annotation { "Feature Type Name" : "Feature", "Feature Type Description" : "" }
export const myFeature = defineFeature(function(context is Context, id is Id, definition is map)
    precondition{}
    {
        {
            var Q0;
            Q0=qCreatedBy(makeId("Front.planeOp"),FACE);
            var sketch = newSketch(context, id + "F0", { "sketchPlane" : qUnion([Q0])});
            skLineSegment(sketch, "E0", {"start": v(0, 0) * mm, "end": v(-4572, 0) * mm});
            skLineSegment(sketch, "E1", {"start": v(0, 0) * mm, "end": v(4572, 0) * mm});
            skLineSegment(sketch, "E2", {"start": v(0, 0) * mm, "end": v(0, 2286) * mm, "construction": true});
            skLineSegment(sketch, "E3", {"start": v(0, 2286) * mm, "end": v(-4572, 0) * mm});
            skLineSegment(sketch, "E4", {"start": v(0, 2286) * mm, "end": v(4572, 0) * mm});
            skLineSegment(sketch, "E5", {"start": v(-4572, 0) * mm, "end": v(-5486.4, 0) * mm});
            skLineSegment(sketch, "E6", {"start": v(-5486.4, 0) * mm, "end": v(0, 2743.2) * mm});
            skLineSegment(sketch, "E7", {"start": v(4572, 0) * mm, "end": v(5486.4, 0) * mm});
            skLineSegment(sketch, "E8", {"start": v(5486.4, 0) * mm, "end": v(0, 2743.2) * mm});
            skLineSegment(sketch, "E9", {"start": v(0, 2286) * mm, "end": v(0, 2743.2) * mm});
            skLineSegment(sketch, "E10", {"start": v(-4572, 0) * mm, "end": v(-4572, -3352.8) * mm});
            skLineSegment(sketch, "E11", {"start": v(-4572, -3352.8) * mm, "end": v(4572, -3352.8) * mm});
            skLineSegment(sketch, "E12", {"start": v(4572, -3352.8) * mm, "end": v(4572, 0) * mm});
            skLineSegment(sketch, "E13", {"start": v(-4572, -3352.8) * mm, "end": v(-4572, -3962.4) * mm});
            skLineSegment(sketch, "E14", {"start": v(-4572, -3962.4) * mm, "end": v(4572, -3962.4) * mm});
            skLineSegment(sketch, "E15", {"start": v(4572, -3962.4) * mm, "end": v(4572, -3352.8) * mm});
            skLineSegment(sketch, "E16", {"start": v(4572, -3352.8) * mm, "end": v(9144, -3352.8) * mm});
            skLineSegment(sketch, "E17", {"start": v(9144, -3352.8) * mm, "end": v(9144, -3962.4) * mm});
            skLineSegment(sketch, "E18", {"start": v(9144, -3962.4) * mm, "end": v(4572, -3962.4) * mm});
            skLineSegment(sketch, "E19.bottom", {"start": v(6096, -1219.2) * mm, "end": v(7315.2, -1219.2) * mm});
            skLineSegment(sketch, "E19.top", {"start": v(6096, -2743.2) * mm, "end": v(7315.2, -2743.2) * mm});
            skLineSegment(sketch, "E19.left", {"start": v(6096, -1219.2) * mm, "end": v(6096, -2743.2) * mm});
            skLineSegment(sketch, "E19.right", {"start": v(7315.2, -1219.2) * mm, "end": v(7315.2, -2743.2) * mm});
            skLineSegment(sketch, "E20", {"start": v(6096, -2743.2) * mm, "end": v(4572, -2743.2) * mm, "construction": true});
            skLineSegment(sketch, "E21", {"start": v(6248.4, -1371.6) * mm, "end": v(7162.8, -1371.6) * mm});
            skLineSegment(sketch, "E22", {"start": v(7162.8, -1371.6) * mm, "end": v(7162.8, -2590.8) * mm});
            skLineSegment(sketch, "E23", {"start": v(7162.8, -2590.8) * mm, "end": v(6248.4, -2590.8) * mm});
            skLineSegment(sketch, "E24", {"start": v(6248.4, -2590.8) * mm, "end": v(6248.4, -1371.6) * mm});
            skLineSegment(sketch, "E25", {"start": v(609.6, -1371.6) * mm, "end": v(3352.8, -1371.6) * mm});
            skLineSegment(sketch, "E26", {"start": v(3352.8, -1371.6) * mm, "end": v(3352.8, -2743.2) * mm});
            skLineSegment(sketch, "E27", {"start": v(3352.8, -2743.2) * mm, "end": v(609.6, -2743.2) * mm});
            skLineSegment(sketch, "E28", {"start": v(609.6, -2743.2) * mm, "end": v(609.6, -1371.6) * mm});
            skLineSegment(sketch, "E29", {"start": v(762, -1524) * mm, "end": v(3200.4, -1524) * mm});
            skLineSegment(sketch, "E30", {"start": v(3200.4, -1524) * mm, "end": v(3200.4, -2590.8) * mm});
            skLineSegment(sketch, "E31", {"start": v(3200.4, -2590.8) * mm, "end": v(762, -2590.8) * mm});
            skLineSegment(sketch, "E32", {"start": v(762, -2590.8) * mm, "end": v(762, -1524) * mm});
            skLineSegment(sketch, "E33", {"start": v(-3352.8, -3352.8) * mm, "end": v(-3352.8, -1219.2) * mm});
            skLineSegment(sketch, "E34", {"start": v(-3352.8, -1219.2) * mm, "end": v(-2438.4, -1219.2) * mm});
            skLineSegment(sketch, "E35", {"start": v(-2438.4, -1219.2) * mm, "end": v(-2438.4, -3352.8) * mm});
            skPoint(sketch, "E35.endSnap0", {"position": v(0, -3352.8) * mm});
            skLineSegment(sketch, "E36", {"start": v(-2438.4, -3352.8) * mm, "end": v(-3352.8, -3352.8) * mm});
            skLineSegment(sketch, "E37", {"start": v(-3657.6, -3352.8) * mm, "end": v(-3657.6, -914.4) * mm});
            skLineSegment(sketch, "E38", {"start": v(-3657.6, -914.4) * mm, "end": v(-2133.6, -914.4) * mm});
            skLineSegment(sketch, "E39", {"start": v(-2133.6, -914.4) * mm, "end": v(-2133.6, -3352.8) * mm});
            skLineSegment(sketch, "E40", {"start": v(-2133.6, -3352.8) * mm, "end": v(-3657.6, -3352.8) * mm});
            skLineSegment(sketch, "E41", {"start": v(9098.34, -1219.69) * mm, "end": v(9144, -3352.8) * mm});
            skLineSegment(sketch, "E42", {"start": v(9098.34, -1219.69) * mm, "end": v(9098.34, -762.49) * mm});
            skLineSegment(sketch, "E43", {"start": v(9098.34, -762.49) * mm, "end": v(4572, 0) * mm});
            skLineSegment(sketch, "E44", {"start": v(6231.62, -279.57) * mm, "end": v(6231.62, -889.17) * mm, "construction": true});
            skLineSegment(sketch, "E45", {"start": v(9101.8, -1381.26) * mm, "end": v(4572, -618.19) * mm});
            skSolve(sketch);
        }
        {
            var Q0;
            Q0=makeQuery(id+"F0.imprint","IMPRINT",FACE,{"disambiguationData":[TD([[makeQuery(id+"F0.imprint","IMPRINT",EDGE,{"derivedFrom":sQuery(id+"F0.wireOp",EDGE,"E0")}),1.0]])]});
            var Q1;
            Q1=makeQuery(id+"F0.imprint","IMPRINT",FACE,{"disambiguationData":[TD([[makeQuery(id+"F0.imprint","IMPRINT",EDGE,{"derivedFrom":sQuery(id+"F0.wireOp",EDGE,"E0")}),-1.0]])]});
            var Q2;
            {var subQ0=sQuery(id+"F0.wireOp",EDGE,"E16");Q2=makeQuery(id+"F0.imprint","IMPRINT",FACE,{"disambiguationData":[TD([[makeQuery(id+"F0.imprint","IMPRINT",EDGE,{"derivedFrom":subQ0}),1.0]])]});}
            extrude(context, id + "F1", {"entities" : qUnion([Q0, Q1, Q2]), "depth" : 3657.6 * mm, "offsetDistance" : 30.48 * mm, "hasSecondDirection" : true, "secondDirectionOppositeDirection" : true, "secondDirectionDepth" : 3657.6 * mm});
        }
        {
            var Q0;
            {var subQ0=sQuery(id+"F0.wireOp",EDGE,"E33");Q0=makeQuery(id+"F0.imprint","IMPRINT",FACE,{"disambiguationData":[TD([[makeQuery(id+"F0.imprint","IMPRINT",EDGE,{"derivedFrom":subQ0}),-1.0]])]});}
            var Q1;
            Q1=makeQuery(id+"F0.imprint","IMPRINT",FACE,{"disambiguationData":[TD([[makeQuery(id+"F0.imprint","IMPRINT",EDGE,{"derivedFrom":sQuery(id+"F0.wireOp",EDGE,"E29")}),-1.0]])]});
            var Q2;
            Q2=makeQuery(id+"F0.imprint","IMPRINT",FACE,{"disambiguationData":[TD([[makeQuery(id+"F0.imprint","IMPRINT",EDGE,{"derivedFrom":sQuery(id+"F0.wireOp",EDGE,"E21")}),-1.0]])]});
            extrude(context, id + "F2", {"entities" : qUnion([Q0, Q1, Q2]), "depth" : 3810 * mm, "offsetDistance" : 30.48 * mm, "hasSecondDirection" : true, "secondDirectionOppositeDirection" : true, "secondDirectionDepth" : 3657.6 * mm});
        }
        {
            var Q0;
            {var subQ2=sQuery(id+"F0.wireOp",EDGE,"E33");Q0=makeQuery(id+"F0.imprint","IMPRINT",FACE,{"disambiguationData":[TD([[makeQuery(id+"F0.imprint","IMPRINT",EDGE,{"derivedFrom":subQ2}),1.0]])]});}
            var Q1;
            Q1=makeQuery(id+"F0.imprint","IMPRINT",FACE,{"disambiguationData":[TD([[makeQuery(id+"F0.imprint","IMPRINT",EDGE,{"derivedFrom":sQuery(id+"F0.wireOp",EDGE,"E25")}),-1.0]])]});
            var Q2;
            Q2=makeQuery(id+"F0.imprint","IMPRINT",FACE,{"disambiguationData":[TD([[makeQuery(id+"F0.imprint","IMPRINT",EDGE,{"derivedFrom":sQuery(id+"F0.wireOp",EDGE,"E19.bottom")}),-1.0]])]});
            extrude(context, id + "F3", {"entities" : qUnion([Q0, Q1, Q2]), "depth" : 3962.4 * mm, "offsetDistance" : 30.48 * mm, "hasSecondDirection" : true, "secondDirectionOppositeDirection" : true, "secondDirectionDepth" : 3657.6 * mm});
        }
        {
            var Q0;
            {var subQ0=sQuery(id+"F0.wireOp",EDGE,"E13");Q0=makeQuery(id+"F0.imprint","IMPRINT",FACE,{"disambiguationData":[TD([[makeQuery(id+"F0.imprint","IMPRINT",EDGE,{"derivedFrom":subQ0}),1.0]])]});}
            var Q1;
            Q1=makeQuery(id+"F0.imprint","IMPRINT",FACE,{"disambiguationData":[TD([[makeQuery(id+"F0.imprint","IMPRINT",EDGE,{"derivedFrom":sQuery(id+"F0.wireOp",EDGE,"E15")}),-1.0]])]});
            extrude(context, id + "F4", {"entities" : qUnion([Q0, Q1]), "depth" : 6096 * mm, "offsetDistance" : 30.48 * mm, "hasSecondDirection" : true, "secondDirectionOppositeDirection" : true, "secondDirectionDepth" : 3657.6 * mm});
        }
        {
            var Q0;
            Q0=makeQuery(id+"F0.imprint","IMPRINT",FACE,{"disambiguationData":[TD([[makeQuery(id+"F0.imprint","IMPRINT",EDGE,{"derivedFrom":sQuery(id+"F0.wireOp",EDGE,"E4")}),1.0]])]});
            var Q1;
            Q1=makeQuery(id+"F0.imprint","IMPRINT",FACE,{"disambiguationData":[TD([[makeQuery(id+"F0.imprint","IMPRINT",EDGE,{"derivedFrom":sQuery(id+"F0.wireOp",EDGE,"E3")}),-1.0]])]});
            extrude(context, id + "F5", {"entities" : qUnion([Q0, Q1]), "operationType" : NewBodyOperationType.ADD, "depth" : 4267.2 * mm, "offsetDistance" : 30.48 * mm, "hasSecondDirection" : true, "secondDirectionOppositeDirection" : true, "secondDirectionDepth" : 4267.2 * mm});
        }
        {
            var Q0;
            Q0=makeQuery(id+"F4.opExtrude","SWEPT_FACE",FACE,{"disambiguationData":[OSD([sQuery(id+"F0.wireOp",EDGE,"E11"),sQuery(id+"F0.wireOp",EDGE,"E16"),sQuery(id+"F0.wireOp",EDGE,"E40")])]});
            var sketch = newSketch(context, id + "F6", { "sketchPlane" : qUnion([Q0])});
            skText(sketch, "E46", { "text": "Vivian Gray", "fontName": "OpenSans-Regular.ttf"});
            const initialGuessF6  = {"E46": [-2.29704, -5.3801, 1, 0, 1.15345]};
            skSetInitialGuess(sketch, initialGuessF6);
            skSolve(sketch);
        }
        {
            var Q0;
            Q0 = qSketchRegion(id + "F6", true);
            extrude(context, id + "F7", {"entities" : qUnion([Q0]), "operationType" : NewBodyOperationType.ADD, "depth" : 609.6 * mm, "offsetDistance" : 30.48 * mm});
        }
        {
            var Q0;
            Q0=makeQuery(id+"F1.opExtrude","SWEPT_FACE",FACE,{"disambiguationData":[OSD([sQuery(id+"F0.wireOp",EDGE,"E41")])]});
            var sketch = newSketch(context, id + "F8", { "sketchPlane" : qUnion([Q0])});
            skLineSegment(sketch, "E47.bottom", {"start": v(-2438.4, -1980.63) * mm, "end": v(-1219.2, -1980.63) * mm});
            skLineSegment(sketch, "E47.top", {"start": v(-2438.4, -2895.03) * mm, "end": v(-1219.2, -2895.03) * mm});
            skLineSegment(sketch, "E47.left", {"start": v(-2438.4, -1980.63) * mm, "end": v(-2438.4, -2895.03) * mm});
            skLineSegment(sketch, "E47.right", {"start": v(-1219.2, -1980.63) * mm, "end": v(-1219.2, -2895.03) * mm});
            skLineSegment(sketch, "E48.bottom", {"start": v(1219.2, -1980.63) * mm, "end": v(2438.4, -1980.63) * mm});
            skLineSegment(sketch, "E48.top", {"start": v(1219.2, -2895.03) * mm, "end": v(2438.4, -2895.03) * mm});
            skLineSegment(sketch, "E48.left", {"start": v(1219.2, -1980.63) * mm, "end": v(1219.2, -2895.03) * mm});
            skLineSegment(sketch, "E48.right", {"start": v(2438.4, -1980.63) * mm, "end": v(2438.4, -2895.03) * mm});
            skLineSegment(sketch, "E49.bottom", {"start": v(-2639.53, -1809.3) * mm, "end": v(-997.6, -1809.3) * mm});
            skLineSegment(sketch, "E49.top", {"start": v(-2639.53, -3084.73) * mm, "end": v(-997.6, -3084.73) * mm});
            skLineSegment(sketch, "E49.left", {"start": v(-2639.53, -1809.3) * mm, "end": v(-2639.53, -3084.73) * mm});
            skLineSegment(sketch, "E49.right", {"start": v(-997.6, -1809.3) * mm, "end": v(-997.6, -3084.73) * mm});
            skLineSegment(sketch, "E50.bottom", {"start": v(983.6, -1831.3) * mm, "end": v(2743.2, -1831.3) * mm});
            skLineSegment(sketch, "E50.top", {"start": v(983.6, -3033.42) * mm, "end": v(2743.2, -3033.42) * mm});
            skLineSegment(sketch, "E50.left", {"start": v(983.6, -1831.3) * mm, "end": v(983.6, -3033.42) * mm});
            skLineSegment(sketch, "E50.right", {"start": v(2743.2, -1831.3) * mm, "end": v(2743.2, -3033.42) * mm});
            skSolve(sketch);
        }
        {
            var Q0;
            Q0=makeQuery(id+"F8.imprint","IMPRINT",FACE,{"disambiguationData":[TD([[makeQuery(id+"F8.imprint","IMPRINT",EDGE,{"derivedFrom":sQuery(id+"F8.wireOp",EDGE,"E48.bottom")}),-1.0]])]});
            var Q1;
            Q1=makeQuery(id+"F8.imprint","IMPRINT",FACE,{"disambiguationData":[TD([[makeQuery(id+"F8.imprint","IMPRINT",EDGE,{"derivedFrom":sQuery(id+"F8.wireOp",EDGE,"E47.bottom")}),-1.0]])]});
            extrude(context, id + "F9", {"entities" : qUnion([Q0, Q1]), "operationType" : NewBodyOperationType.ADD, "depth" : 152.4 * mm, "offsetDistance" : 30.48 * mm});
        }
        {
            var Q0;
            Q0 = qSketchRegion(id + "F8", true);
            extrude(context, id + "F10", {"entities" : qUnion([Q0]), "operationType" : NewBodyOperationType.ADD, "depth" : 304.8 * mm, "offsetDistance" : 30.48 * mm});
        }
    });